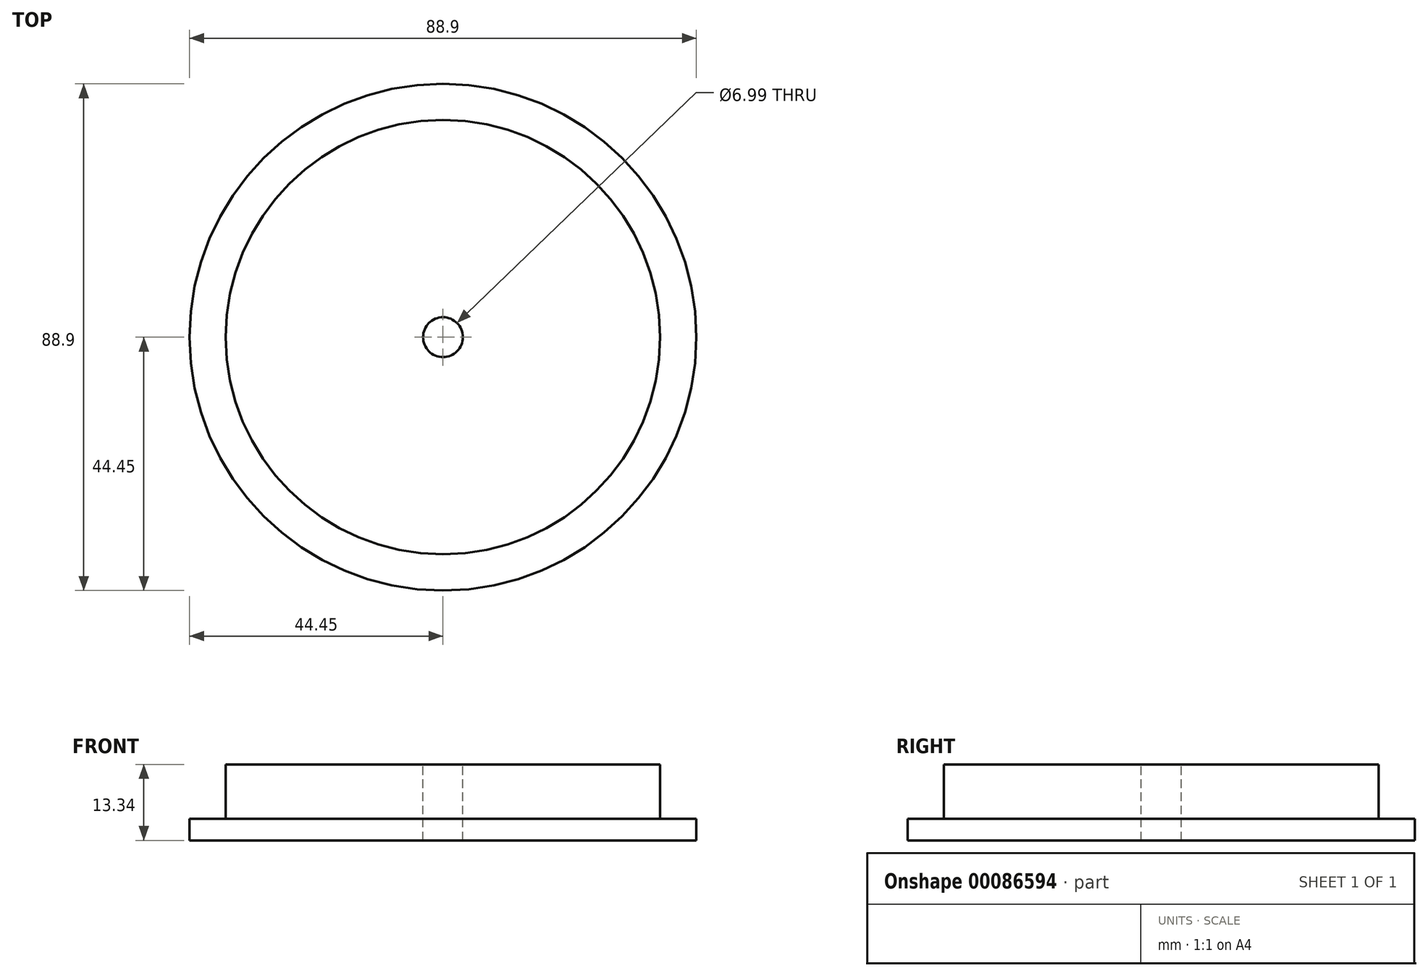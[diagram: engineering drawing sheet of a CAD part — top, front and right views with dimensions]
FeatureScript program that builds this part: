
annotation { "Feature Type Name" : "Feature", "Feature Type Description" : "" }
export const myFeature = defineFeature(function(context is Context, id is Id, definition is map)
    precondition{}
    {
        {
            var Q0;
            Q0=qCreatedBy(makeId("Top.planeOp"),FACE);
            var sketch = newSketch(context, id + "F0", { "sketchPlane" : qUnion([Q0])});
            skCircle(sketch, "E0", {"center": v(0, 0) * mm, "radius": 44.45 * mm});
            skSolve(sketch);
        }
        {
            var Q0;
            Q0=makeQuery(id+"F0.imprint","IMPRINT",FACE,{"disambiguationData":[TD([[makeQuery(id+"F0.imprint","IMPRINT",EDGE,{"derivedFrom":sQuery(id+"F0.wireOp",EDGE,"E0")}),1.0]])]});
            extrude(context, id + "F1", {"entities" : qUnion([Q0]), "depth" : 3.8 * mm});
        }
        {
            var Q0;
            Q0=makeQuery(id+"F1.opExtrude","CAP_FACE",FACE,{"disambiguationData":[OSD([sQuery(id+"F0.wireOp",EDGE,"E0")])],"isStart":false});
            var sketch = newSketch(context, id + "F2", { "sketchPlane" : qUnion([Q0])});
            skCircle(sketch, "E1", {"center": v(0, 0) * mm, "radius": 38.1 * mm});
            skSolve(sketch);
        }
        {
            var Q0;
            Q0 = qSketchRegion(id + "F2", true);
            extrude(context, id + "F3", {"entities" : qUnion([Q0]), "operationType" : NewBodyOperationType.ADD, "depth" : 9.52 * mm});
        }
        {
            var Q0;
            Q0=makeQuery(id+"F3.opExtrude","CAP_FACE",FACE,{"disambiguationData":[OSD([sQuery(id+"F2.wireOp",EDGE,"E1")])],"isStart":false});
            var sketch = newSketch(context, id + "F4", { "sketchPlane" : qUnion([Q0])});
            skCircle(sketch, "E2", {"center": v(0, 0) * mm, "radius": 3.5 * mm});
            skSolve(sketch);
        }
        {
            var Q0;
            Q0=sQuery(id+"F4.wireOp",VERTEX,"E2.center");
            var Q1;
            Q1=makeQuery(id+"F1.opExtrude","SWEPT_BODY",BODY,{"disambiguationData":[OSD([sQuery(id+"F0.wireOp",EDGE,"E0")])]});
            hole(context, id + "F5", {"style" : HoleStyle.SIMPLE, "endStyle" : HoleEndStyle.THROUGH, "holeDiameter" : 7 * mm, "locations" : qUnion([Q0]), "scope" : qUnion([Q1]), "isTappedThrough" : true});
        }
    });
